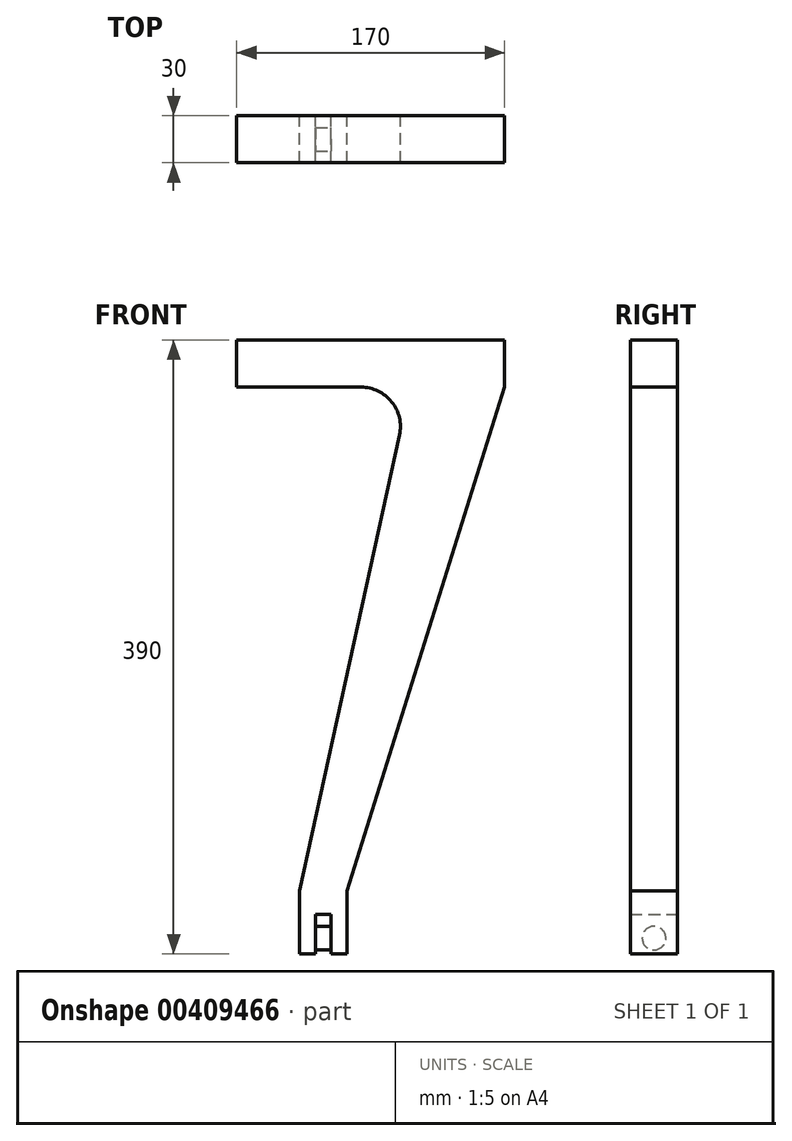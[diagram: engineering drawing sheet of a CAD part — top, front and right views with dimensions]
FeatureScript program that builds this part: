
annotation { "Feature Type Name" : "Feature", "Feature Type Description" : "" }
export const myFeature = defineFeature(function(context is Context, id is Id, definition is map)
    precondition{}
    {
        {
            var Q0;
            Q0=qCreatedBy(makeId("Front.planeOp"),FACE);
            var sketch = newSketch(context, id + "F0", { "sketchPlane" : qUnion([Q0])});
            skLineSegment(sketch, "E0", {"start": v(0, 55.41) * mm, "end": v(0, -66.88) * mm, "construction": true});
            skLineSegment(sketch, "E1", {"start": v(103.36, 319.66) * mm, "end": v(40, 30) * mm});
            skLineSegment(sketch, "E2", {"start": v(40, 30) * mm, "end": v(40, 0) * mm});
            skLineSegment(sketch, "E3", {"start": v(40, 0) * mm, "end": v(70, 0) * mm, "construction": true});
            skLineSegment(sketch, "E4", {"start": v(70, 0) * mm, "end": v(70, 30) * mm});
            skLineSegment(sketch, "E5", {"start": v(70, 30) * mm, "end": v(170, 350) * mm});
            skLineSegment(sketch, "E6", {"start": v(170, 350) * mm, "end": v(170, 380) * mm});
            skLineSegment(sketch, "E7", {"start": v(170, 380) * mm, "end": v(0, 380) * mm});
            skLineSegment(sketch, "E8", {"start": v(70, 30) * mm, "end": v(40, 30) * mm, "construction": true});
            skLineSegment(sketch, "E9", {"start": v(78.94, 350) * mm, "end": v(0, 350) * mm});
            skLineSegment(sketch, "E10", {"start": v(170, 350) * mm, "end": v(110, 350) * mm, "construction": true});
            skLineSegment(sketch, "E11", {"start": v(40, 0) * mm, "end": v(40, -10) * mm});
            skLineSegment(sketch, "E12", {"start": v(40, -10) * mm, "end": v(50, -10) * mm});
            skLineSegment(sketch, "E13", {"start": v(70, -10) * mm, "end": v(70, 0) * mm});
            skLineSegment(sketch, "E14", {"start": v(0, 350) * mm, "end": v(0, 380) * mm});
            skPoint(sketch, "E15.visualSharp", {"position": v(110, 350) * mm});
            skArc(sketch, "E15.filletArc", {"start": v(103.36, 319.66) * mm, "mid": v(98.42, 340.68) * mm, "end": v(78.94, 350) * mm});
            skLineSegment(sketch, "E16", {"start": v(60, -10) * mm, "end": v(60, 15) * mm});
            skLineSegment(sketch, "E17", {"start": v(60, 15) * mm, "end": v(50, 15) * mm});
            skLineSegment(sketch, "E18", {"start": v(50, 15) * mm, "end": v(50, -10) * mm});
            skLineSegment(sketch, "E19.trimOffspring", {"start": v(60, -10) * mm, "end": v(70, -10) * mm});
            skSolve(sketch);
        }
        {
            var Q0;
            Q0=makeQuery(id+"F0.imprint","IMPRINT",FACE,{"disambiguationData":[TD([[makeQuery(id+"F0.imprint","IMPRINT",EDGE,{"derivedFrom":sQuery(id+"F0.wireOp",EDGE,"E1")}),1.0]])]});
            extrude(context, id + "F1", {"entities" : qUnion([Q0]), "depth" : 30 * mm});
        }
        {
            var Q0;
            Q0=makeQuery(id+"F1.opExtrude","SWEPT_FACE",FACE,{"disambiguationData":[OSD([sQuery(id+"F0.wireOp",EDGE,"E4"),sQuery(id+"F0.wireOp",EDGE,"E13")])]});
            var sketch = newSketch(context, id + "F2", { "sketchPlane" : qUnion([Q0])});
            skCircle(sketch, "E20", {"center": v(-15, 0) * mm, "radius": 7.5 * mm});
            skSolve(sketch);
        }
        {
            var Q0;
            Q0 = qSketchRegion(id + "F2", true);
            extrude(context, id + "F3", {"entities" : qUnion([Q0]), "operationType" : NewBodyOperationType.ADD, "oppositeDirection" : true, "depth" : 22.9 * mm});
        }
    });
